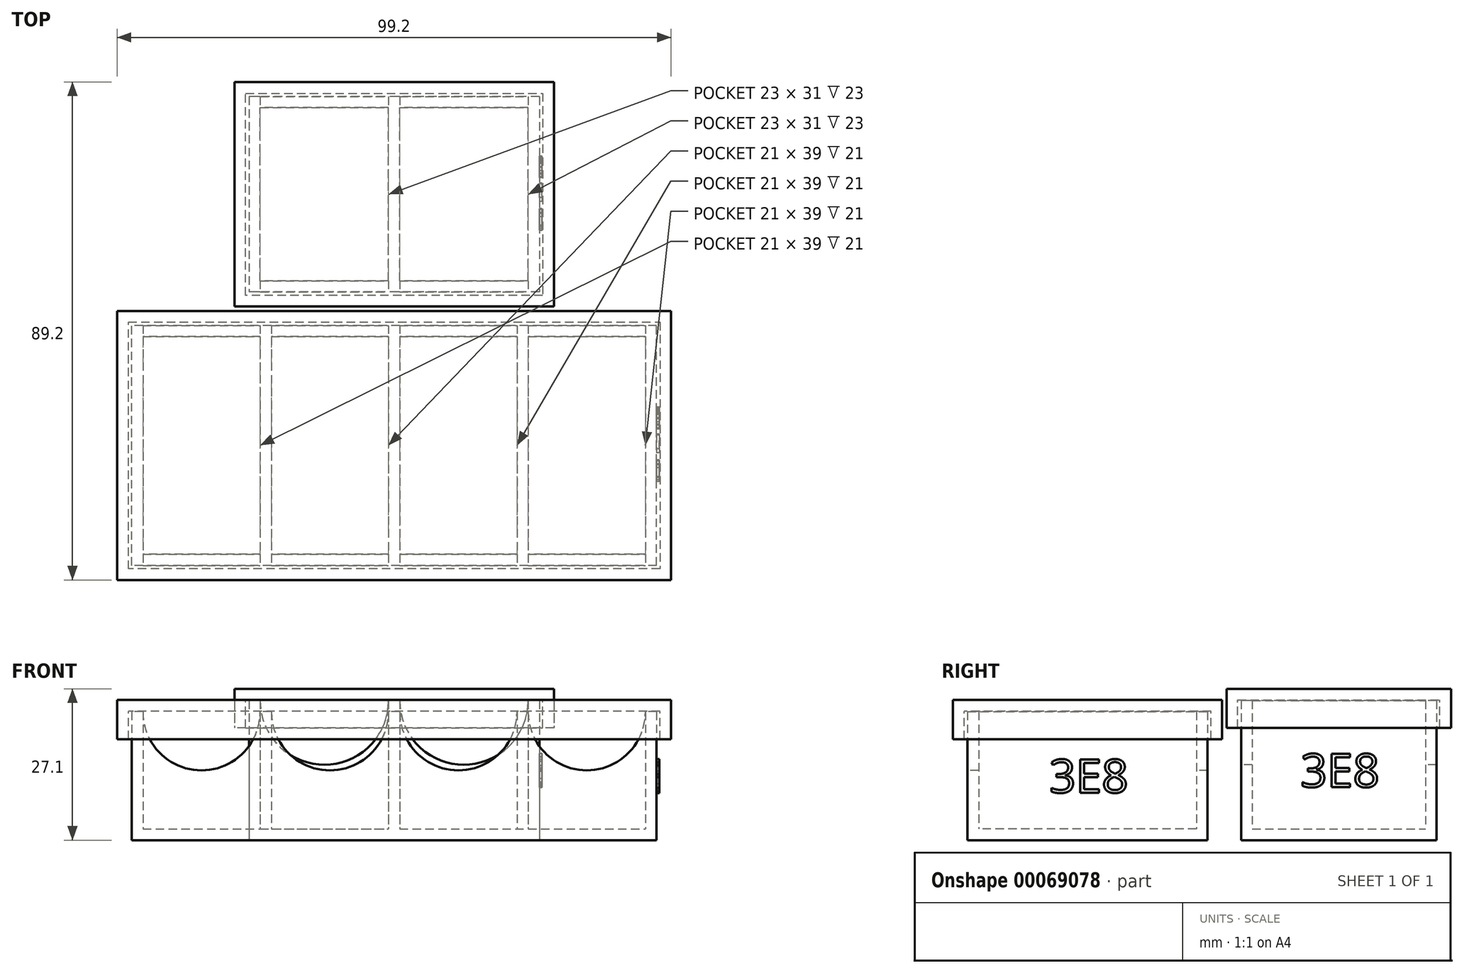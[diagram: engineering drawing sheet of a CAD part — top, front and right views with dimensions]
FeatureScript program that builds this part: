
annotation { "Feature Type Name" : "Feature", "Feature Type Description" : "" }
export const myFeature = defineFeature(function(context is Context, id is Id, definition is map)
    precondition{}
    {
        {
            var Q0;
            Q0=qCreatedBy(makeId("Top.planeOp"),FACE);
            var sketch = newSketch(context, id + "F0", { "sketchPlane" : qUnion([Q0])});
            skLineSegment(sketch, "E0.rect.bottom", {"start": v(47, -21.5) * mm, "end": v(-47, -21.5) * mm});
            skLineSegment(sketch, "E0.rect.top", {"start": v(47, 21.5) * mm, "end": v(-47, 21.5) * mm});
            skLineSegment(sketch, "E0.rect.left", {"start": v(47, -21.5) * mm, "end": v(47, 21.5) * mm});
            skLineSegment(sketch, "E0.rect.right", {"start": v(-47, -21.5) * mm, "end": v(-47, 21.5) * mm});
            skPoint(sketch, "E0.rect.middle", {"position": v(0, 0) * mm});
            skLineSegment(sketch, "E1", {"start": v(0, 0) * mm, "end": v(0, 45) * mm, "construction": true});
            skLineSegment(sketch, "E2.rect.bottom", {"start": v(26, 62.5) * mm, "end": v(-26, 62.5) * mm});
            skLineSegment(sketch, "E2.rect.top", {"start": v(26, 27.5) * mm, "end": v(-26, 27.5) * mm});
            skLineSegment(sketch, "E2.rect.left", {"start": v(26, 62.5) * mm, "end": v(26, 27.5) * mm});
            skLineSegment(sketch, "E2.rect.right", {"start": v(-26, 62.5) * mm, "end": v(-26, 27.5) * mm});
            skPoint(sketch, "E2.rect.middle", {"position": v(0, 45) * mm});
            skSolve(sketch);
        }
        {
            var Q0;
            Q0=qSketchRegion(id+"F0",true);
            extrude(context, id + "F1", {"entities" : qUnion([Q0]), "depth" : 2 * mm});
        }
        {
            var Q0;
            Q0=makeQuery(id+"F1.opExtrude","CAP_FACE",FACE,{"disambiguationData":[OSD([sQuery(id+"F0.wireOp",EDGE,"E0.rect.bottom"),sQuery(id+"F0.wireOp",EDGE,"E0.rect.top"),sQuery(id+"F0.wireOp",EDGE,"E0.rect.left"),sQuery(id+"F0.wireOp",EDGE,"E0.rect.right")])],"isStart":false});
            var sketch = newSketch(context, id + "F2", { "sketchPlane" : qUnion([Q0])});
            skLineSegment(sketch, "E3.0.0", {"start": v(-47, -21.5) * mm, "end": v(47, -21.5) * mm});
            skLineSegment(sketch, "E3.0.1", {"start": v(47, -21.5) * mm, "end": v(47, 21.5) * mm});
            skLineSegment(sketch, "E3.0.2", {"start": v(47, 21.5) * mm, "end": v(-47, 21.5) * mm});
            skLineSegment(sketch, "E3.0.3", {"start": v(-47, 21.5) * mm, "end": v(-47, -21.5) * mm});
            skLineSegment(sketch, "E4", {"start": v(-47, 0) * mm, "end": v(-45, 0) * mm, "construction": true});
            skLineSegment(sketch, "E5.bottom", {"start": v(-45, 19.5) * mm, "end": v(-24, 19.5) * mm});
            skLineSegment(sketch, "E5.top", {"start": v(-45, -19.5) * mm, "end": v(-24, -19.5) * mm});
            skLineSegment(sketch, "E5.left", {"start": v(-45, 19.5) * mm, "end": v(-45, -19.5) * mm});
            skLineSegment(sketch, "E5.right", {"start": v(-24, 19.5) * mm, "end": v(-24, -19.5) * mm});
            skLineSegment(sketch, "E6.1.0.0", {"start": v(-1, 19.5) * mm, "end": v(-1, -19.5) * mm});
            skLineSegment(sketch, "E6.1.0.1", {"start": v(-22, 19.5) * mm, "end": v(-1, 19.5) * mm});
            skLineSegment(sketch, "E6.1.0.2", {"start": v(-22, 19.5) * mm, "end": v(-22, -19.5) * mm});
            skLineSegment(sketch, "E6.1.0.3", {"start": v(-22, -19.5) * mm, "end": v(-1, -19.5) * mm});
            skLineSegment(sketch, "E6.2.0.0", {"start": v(22, 19.5) * mm, "end": v(22, -19.5) * mm});
            skLineSegment(sketch, "E6.2.0.1", {"start": v(1, 19.5) * mm, "end": v(22, 19.5) * mm});
            skLineSegment(sketch, "E6.2.0.2", {"start": v(1, 19.5) * mm, "end": v(1, -19.5) * mm});
            skLineSegment(sketch, "E6.2.0.3", {"start": v(1, -19.5) * mm, "end": v(22, -19.5) * mm});
            skLineSegment(sketch, "E6.3.0.0", {"start": v(45, 19.5) * mm, "end": v(45, -19.5) * mm});
            skLineSegment(sketch, "E6.3.0.1", {"start": v(24, 19.5) * mm, "end": v(45, 19.5) * mm});
            skLineSegment(sketch, "E6.3.0.2", {"start": v(24, 19.5) * mm, "end": v(24, -19.5) * mm});
            skLineSegment(sketch, "E6.3.0.3", {"start": v(24, -19.5) * mm, "end": v(45, -19.5) * mm});
            skLineSegment(sketch, "E6.direction1", {"start": v(-24, -19.5) * mm, "end": v(-1, -19.5) * mm, "construction": true});
            skSolve(sketch);
        }
        {
            var Q0;
            Q0=qSketchRegion(id+"F2",true);
            extrude(context, id + "F3", {"entities" : qUnion([Q0]), "operationType" : NewBodyOperationType.ADD, "depth" : 21 * mm});
        }
        {
            var Q0;
            Q0=makeQuery(id+"F3.boolean.opBoolean","MERGE",FACE,{"derivedFrom":[makeQuery(id+"F1.opExtrude","SWEPT_FACE",FACE,{"disambiguationData":[OSD([sQuery(id+"F0.wireOp",EDGE,"E0.rect.bottom")])]}),makeQuery(id+"F3.opExtrude","SWEPT_FACE",FACE,{"disambiguationData":[OSD([sQuery(id+"F2.wireOp",EDGE,"E3.0.0")])]})]});
            var sketch = newSketch(context, id + "F4", { "sketchPlane" : qUnion([Q0])});
            skPoint(sketch, "E7.0", {"position": v(-45, 23) * mm});
            skPoint(sketch, "E8.0", {"position": v(-24, 23) * mm});
            skLineSegment(sketch, "E9", {"start": v(-45, 23) * mm, "end": v(-24, 23) * mm});
            skArc(sketch, "E10", {"start": v(-45, 23) * mm, "mid": v(-34.5, 12.5) * mm, "end": v(-24, 23) * mm});
            skLineSegment(sketch, "E11.1.0.0", {"start": v(-22, 23) * mm, "end": v(-1, 23) * mm});
            skArc(sketch, "E11.1.0.1", {"start": v(-22, 23) * mm, "mid": v(-11.5, 12.5) * mm, "end": v(-1, 23) * mm});
            skLineSegment(sketch, "E11.2.0.0", {"start": v(1, 23) * mm, "end": v(22, 23) * mm});
            skArc(sketch, "E11.2.0.1", {"start": v(1, 23) * mm, "mid": v(11.5, 12.5) * mm, "end": v(22, 23) * mm});
            skLineSegment(sketch, "E11.3.0.0", {"start": v(24, 23) * mm, "end": v(45, 23) * mm});
            skArc(sketch, "E11.3.0.1", {"start": v(24, 23) * mm, "mid": v(34.5, 12.5) * mm, "end": v(45, 23) * mm});
            skLineSegment(sketch, "E11.direction1", {"start": v(-45, 23) * mm, "end": v(-22, 23) * mm, "construction": true});
            skSolve(sketch);
        }
        {
            var Q0;
            Q0=qSketchRegion(id+"F4",true);
            extrude(context, id + "F5", {"entities" : qUnion([Q0]), "operationType" : NewBodyOperationType.REMOVE, "endBound" : BoundingType.THROUGH_ALL, "oppositeDirection" : true, "depth" : 25 * mm});
        }
        {
            var Q0;
            {var subQ0=sQuery(id+"F2.wireOp",EDGE,"E3.0.0");var subQ1=sQuery(id+"F2.wireOp",EDGE,"E5.bottom");var subQ2=sQuery(id+"F2.wireOp",EDGE,"E3.0.2");var subQ3=sQuery(id+"F2.wireOp",EDGE,"E3.0.3");var subQ4=sQuery(id+"F2.wireOp",EDGE,"E5.top");var subQ5=sQuery(id+"F2.wireOp",EDGE,"E5.left");Q0=makeQuery(id+"F5.boolean.opBoolean","SPLIT",FACE,{"disambiguationData":[TD([makeQuery(id+"F1.opExtrude","SWEPT_FACE",FACE,{"disambiguationData":[OSD([sQuery(id+"F0.wireOp",EDGE,"E0.rect.right")])]})])],"derivedFrom":makeQuery(id+"F3.opExtrude","CAP_FACE",FACE,{"disambiguationData":[OSD([subQ0,sQuery(id+"F2.wireOp",EDGE,"E3.0.1"),subQ2,subQ3,subQ1,subQ4,subQ5,sQuery(id+"F2.wireOp",EDGE,"E5.right"),sQuery(id+"F2.wireOp",EDGE,"E6.1.0.0"),sQuery(id+"F2.wireOp",EDGE,"E6.1.0.1"),sQuery(id+"F2.wireOp",EDGE,"E6.1.0.2"),sQuery(id+"F2.wireOp",EDGE,"E6.1.0.3"),sQuery(id+"F2.wireOp",EDGE,"E6.2.0.0"),sQuery(id+"F2.wireOp",EDGE,"E6.2.0.1"),sQuery(id+"F2.wireOp",EDGE,"E6.2.0.2"),sQuery(id+"F2.wireOp",EDGE,"E6.2.0.3"),sQuery(id+"F2.wireOp",EDGE,"E6.3.0.0"),sQuery(id+"F2.wireOp",EDGE,"E6.3.0.1"),sQuery(id+"F2.wireOp",EDGE,"E6.3.0.2"),sQuery(id+"F2.wireOp",EDGE,"E6.3.0.3"),sQuery(id+"F2.wireOp",EDGE,"E6.4.0.0"),sQuery(id+"F2.wireOp",EDGE,"E6.4.0.1"),sQuery(id+"F2.wireOp",EDGE,"E6.4.0.2"),sQuery(id+"F2.wireOp",EDGE,"E6.4.0.3"),sQuery(id+"F2.wireOp",EDGE,"E6.5.0.0"),sQuery(id+"F2.wireOp",EDGE,"E6.5.0.1"),sQuery(id+"F2.wireOp",EDGE,"E6.5.0.2"),sQuery(id+"F2.wireOp",EDGE,"E6.5.0.3")])],"isStart":false})});}
            cPlane(context, id + "F6", {"entities" : qUnion([Q0]), "cplaneType" : CPlaneType.OFFSET, "offset" : .1 * mm, "width" : 150 * mm, "height" : 150 * mm});
        }
        {
            var Q0;
            Q0=qCreatedBy(id+"F6.planeOp",FACE);
            var sketch = newSketch(context, id + "F7", { "sketchPlane" : qUnion([Q0])});
            skLineSegment(sketch, "E12.0.0", {"start": v(47, -21.5) * mm, "end": v(-47, -21.5) * mm, "construction": true});
            skLineSegment(sketch, "E12.0.1", {"start": v(-47, -21.5) * mm, "end": v(-47, 21.5) * mm, "construction": true});
            skLineSegment(sketch, "E12.0.2", {"start": v(-47, 21.5) * mm, "end": v(47, 21.5) * mm});
            skLineSegment(sketch, "E12.0.3", {"start": v(47, 21.5) * mm, "end": v(47, -21.5) * mm, "construction": true});
            skLineSegment(sketch, "E13.0", {"start": v(-49.6, 24.1) * mm, "end": v(49.6, 24.1) * mm});
            skLineSegment(sketch, "E13.1", {"start": v(-49.6, -24.1) * mm, "end": v(-49.6, 24.1) * mm});
            skLineSegment(sketch, "E13.2", {"start": v(49.6, -24.1) * mm, "end": v(-49.6, -24.1) * mm});
            skLineSegment(sketch, "E13.3", {"start": v(49.6, 24.1) * mm, "end": v(49.6, -24.1) * mm});
            skSolve(sketch);
        }
        {
            var Q0;
            Q0=qSketchRegion(id+"F7",true);
            extrude(context, id + "F8", {"entities" : qUnion([Q0]), "depth" : 2 * mm});
        }
        {
            var Q0;
            Q0=makeQuery(id+"F8.opExtrude","CAP_FACE",FACE,{"disambiguationData":[OSD([sQuery(id+"F7.wireOp",EDGE,"E13.0"),sQuery(id+"F7.wireOp",EDGE,"E13.1"),sQuery(id+"F7.wireOp",EDGE,"E13.2"),sQuery(id+"F7.wireOp",EDGE,"E13.3")])],"isStart":true});
            var sketch = newSketch(context, id + "F9", { "sketchPlane" : qUnion([Q0])});
            skLineSegment(sketch, "E14.0.0", {"start": v(-49.6, -24.1) * mm, "end": v(49.6, -24.1) * mm});
            skLineSegment(sketch, "E14.0.1", {"start": v(49.6, -24.1) * mm, "end": v(49.6, 24.1) * mm});
            skLineSegment(sketch, "E14.0.2", {"start": v(49.6, 24.1) * mm, "end": v(-49.6, 24.1) * mm});
            skLineSegment(sketch, "E14.0.3", {"start": v(-49.6, 24.1) * mm, "end": v(-49.6, -24.1) * mm});
            skLineSegment(sketch, "E15.0", {"start": v(47.6, 22.1) * mm, "end": v(-47.6, 22.1) * mm});
            skLineSegment(sketch, "E15.1", {"start": v(47.6, -22.1) * mm, "end": v(47.6, 22.1) * mm});
            skLineSegment(sketch, "E15.2", {"start": v(-47.6, -22.1) * mm, "end": v(47.6, -22.1) * mm});
            skLineSegment(sketch, "E15.3", {"start": v(-47.6, 22.1) * mm, "end": v(-47.6, -22.1) * mm});
            skSolve(sketch);
        }
        {
            var Q0;
            Q0=qSketchRegion(id+"F9",true);
            extrude(context, id + "F10", {"entities" : qUnion([Q0]), "operationType" : NewBodyOperationType.ADD, "depth" : 5 * mm});
        }
        {
            var Q0;
            Q0=makeQuery(id+"F1.opExtrude","CAP_FACE",FACE,{"disambiguationData":[OSD([sQuery(id+"F0.wireOp",EDGE,"E2.rect.bottom"),sQuery(id+"F0.wireOp",EDGE,"E2.rect.top"),sQuery(id+"F0.wireOp",EDGE,"E2.rect.left"),sQuery(id+"F0.wireOp",EDGE,"E2.rect.right")])],"isStart":false});
            var sketch = newSketch(context, id + "F11", { "sketchPlane" : qUnion([Q0])});
            skLineSegment(sketch, "E16.0.0", {"start": v(26, 27.5) * mm, "end": v(26, 62.5) * mm});
            skLineSegment(sketch, "E16.0.1", {"start": v(26, 62.5) * mm, "end": v(-26, 62.5) * mm});
            skLineSegment(sketch, "E16.0.2", {"start": v(-26, 62.5) * mm, "end": v(-26, 27.5) * mm});
            skLineSegment(sketch, "E16.0.3", {"start": v(-26, 27.5) * mm, "end": v(26, 27.5) * mm});
            skLineSegment(sketch, "E17", {"start": v(-26, 45) * mm, "end": v(-24, 45) * mm, "construction": true});
            skLineSegment(sketch, "E18.bottom", {"start": v(-24, 29.5) * mm, "end": v(-1, 29.5) * mm});
            skLineSegment(sketch, "E18.top", {"start": v(-24, 60.5) * mm, "end": v(-1, 60.5) * mm});
            skLineSegment(sketch, "E18.left", {"start": v(-24, 29.5) * mm, "end": v(-24, 60.5) * mm});
            skLineSegment(sketch, "E18.right", {"start": v(-1, 29.5) * mm, "end": v(-1, 60.5) * mm});
            skLineSegment(sketch, "E19.1.0.0", {"start": v(1, 29.5) * mm, "end": v(24, 29.5) * mm});
            skLineSegment(sketch, "E19.1.0.1", {"start": v(1, 29.5) * mm, "end": v(1, 60.5) * mm});
            skLineSegment(sketch, "E19.1.0.2", {"start": v(1, 60.5) * mm, "end": v(24, 60.5) * mm});
            skLineSegment(sketch, "E19.1.0.3", {"start": v(24, 29.5) * mm, "end": v(24, 60.5) * mm});
            skLineSegment(sketch, "E19.direction1", {"start": v(-24, 29.5) * mm, "end": v(1, 29.5) * mm, "construction": true});
            skSolve(sketch);
        }
        {
            var Q0;
            Q0=qSketchRegion(id+"F11",true);
            extrude(context, id + "F12", {"entities" : qUnion([Q0]), "operationType" : NewBodyOperationType.ADD, "depth" : 23 * mm});
        }
        {
            var Q0;
            Q0=makeQuery(id+"F12.boolean.opBoolean","MERGE",FACE,{"derivedFrom":[makeQuery(id+"F1.opExtrude","SWEPT_FACE",FACE,{"disambiguationData":[OSD([sQuery(id+"F0.wireOp",EDGE,"E2.rect.top")])]}),makeQuery(id+"F12.opExtrude","SWEPT_FACE",FACE,{"disambiguationData":[OSD([sQuery(id+"F11.wireOp",EDGE,"E16.0.3")])]})]});
            var sketch = newSketch(context, id + "F13", { "sketchPlane" : qUnion([Q0])});
            skPoint(sketch, "E20.0", {"position": v(-24, 25) * mm});
            skPoint(sketch, "E21.0", {"position": v(-1, 25) * mm});
            skLineSegment(sketch, "E22", {"start": v(-24, 25) * mm, "end": v(-1, 25) * mm});
            skArc(sketch, "E23", {"start": v(-24, 25) * mm, "mid": v(-12.5, 13.5) * mm, "end": v(-1, 25) * mm});
            skArc(sketch, "E24.1.0.0", {"start": v(1, 25) * mm, "mid": v(12.5, 13.5) * mm, "end": v(24, 25) * mm});
            skLineSegment(sketch, "E24.1.0.1", {"start": v(1, 25) * mm, "end": v(24, 25) * mm});
            skLineSegment(sketch, "E24.direction1", {"start": v(-24, 25) * mm, "end": v(1, 25) * mm, "construction": true});
            skSolve(sketch);
        }
        {
            var Q0;
            Q0=qSketchRegion(id+"F13",true);
            extrude(context, id + "F14", {"entities" : qUnion([Q0]), "operationType" : NewBodyOperationType.REMOVE, "endBound" : BoundingType.THROUGH_ALL, "oppositeDirection" : true, "depth" : 25 * mm});
        }
        {
            var Q0;
            {var subQ0=sQuery(id+"F11.wireOp",EDGE,"E16.0.1");var subQ1=sQuery(id+"F11.wireOp",EDGE,"E18.bottom");var subQ2=sQuery(id+"F11.wireOp",EDGE,"E18.top");var subQ3=sQuery(id+"F11.wireOp",EDGE,"E18.left");var subQ4=sQuery(id+"F11.wireOp",EDGE,"E16.0.2");var subQ5=sQuery(id+"F11.wireOp",EDGE,"E16.0.3");Q0=makeQuery(id+"F14.boolean.opBoolean","SPLIT",FACE,{"disambiguationData":[TD([makeQuery(id+"F1.opExtrude","SWEPT_FACE",FACE,{"disambiguationData":[OSD([sQuery(id+"F0.wireOp",EDGE,"E2.rect.right")])]})])],"derivedFrom":makeQuery(id+"F12.opExtrude","CAP_FACE",FACE,{"disambiguationData":[OSD([sQuery(id+"F11.wireOp",EDGE,"E16.0.0"),subQ0,subQ4,subQ5,subQ1,subQ2,subQ3,sQuery(id+"F11.wireOp",EDGE,"E18.right"),sQuery(id+"F11.wireOp",EDGE,"E19.1.0.0"),sQuery(id+"F11.wireOp",EDGE,"E19.1.0.1"),sQuery(id+"F11.wireOp",EDGE,"E19.1.0.2"),sQuery(id+"F11.wireOp",EDGE,"E19.1.0.3"),sQuery(id+"F11.wireOp",EDGE,"E19.2.0.0"),sQuery(id+"F11.wireOp",EDGE,"E19.2.0.1"),sQuery(id+"F11.wireOp",EDGE,"E19.2.0.2"),sQuery(id+"F11.wireOp",EDGE,"E19.2.0.3"),sQuery(id+"F11.wireOp",EDGE,"E19.3.0.0"),sQuery(id+"F11.wireOp",EDGE,"E19.3.0.1"),sQuery(id+"F11.wireOp",EDGE,"E19.3.0.2"),sQuery(id+"F11.wireOp",EDGE,"E19.3.0.3")])],"isStart":false})});}
            cPlane(context, id + "F15", {"entities" : qUnion([Q0]), "cplaneType" : CPlaneType.OFFSET, "offset" : .1 * mm, "width" : 150 * mm, "height" : 150 * mm});
        }
        {
            var Q0;
            Q0=qCreatedBy(id+"F15.planeOp",FACE);
            var sketch = newSketch(context, id + "F16", { "sketchPlane" : qUnion([Q0])});
            skLineSegment(sketch, "E25.0.0", {"start": v(26, 62.5) * mm, "end": v(26, 27.5) * mm, "construction": true});
            skLineSegment(sketch, "E25.0.1", {"start": v(26, 27.5) * mm, "end": v(-26, 27.5) * mm, "construction": true});
            skLineSegment(sketch, "E25.0.2", {"start": v(-26, 27.5) * mm, "end": v(-26, 62.5) * mm, "construction": true});
            skLineSegment(sketch, "E25.0.3", {"start": v(-26, 62.5) * mm, "end": v(26, 62.5) * mm, "construction": true});
            skLineSegment(sketch, "E26.0", {"start": v(-28.6, 24.9) * mm, "end": v(-28.6, 65.1) * mm});
            skLineSegment(sketch, "E26.1", {"start": v(28.6, 24.9) * mm, "end": v(-28.6, 24.9) * mm});
            skLineSegment(sketch, "E26.2", {"start": v(28.6, 65.1) * mm, "end": v(28.6, 24.9) * mm});
            skLineSegment(sketch, "E26.3", {"start": v(-28.6, 65.1) * mm, "end": v(28.6, 65.1) * mm});
            skSolve(sketch);
        }
        {
            var Q0;
            Q0=qSketchRegion(id+"F16",true);
            extrude(context, id + "F17", {"entities" : qUnion([Q0]), "depth" : 2 * mm});
        }
        {
            var Q0;
            Q0=makeQuery(id+"F17.opExtrude","CAP_FACE",FACE,{"disambiguationData":[OSD([sQuery(id+"F16.wireOp",EDGE,"E26.0"),sQuery(id+"F16.wireOp",EDGE,"E26.1"),sQuery(id+"F16.wireOp",EDGE,"E26.2"),sQuery(id+"F16.wireOp",EDGE,"E26.3")])],"isStart":true});
            var sketch = newSketch(context, id + "F18", { "sketchPlane" : qUnion([Q0])});
            skLineSegment(sketch, "E27.0.0", {"start": v(-28.6, -24.9) * mm, "end": v(-28.6, -65.1) * mm});
            skLineSegment(sketch, "E27.0.1", {"start": v(-28.6, -65.1) * mm, "end": v(28.6, -65.1) * mm});
            skLineSegment(sketch, "E27.0.2", {"start": v(28.6, -65.1) * mm, "end": v(28.6, -24.9) * mm});
            skLineSegment(sketch, "E27.0.3", {"start": v(28.6, -24.9) * mm, "end": v(-28.6, -24.9) * mm});
            skLineSegment(sketch, "E28.0", {"start": v(-26.6, -63.1) * mm, "end": v(26.6, -63.1) * mm});
            skLineSegment(sketch, "E28.1", {"start": v(-26.6, -26.9) * mm, "end": v(-26.6, -63.1) * mm});
            skLineSegment(sketch, "E28.2", {"start": v(26.6, -26.9) * mm, "end": v(-26.6, -26.9) * mm});
            skLineSegment(sketch, "E28.3", {"start": v(26.6, -63.1) * mm, "end": v(26.6, -26.9) * mm});
            skSolve(sketch);
        }
        {
            var Q0;
            Q0=qSketchRegion(id+"F18",true);
            extrude(context, id + "F19", {"entities" : qUnion([Q0]), "operationType" : NewBodyOperationType.ADD, "depth" : 5 * mm});
        }
        {
            var Q0;
            Q0=makeQuery(id+"F3.boolean.opBoolean","MERGE",FACE,{"derivedFrom":[makeQuery(id+"F1.opExtrude","SWEPT_FACE",FACE,{"disambiguationData":[OSD([sQuery(id+"F0.wireOp",EDGE,"E0.rect.left")])]}),makeQuery(id+"F3.opExtrude","SWEPT_FACE",FACE,{"disambiguationData":[OSD([sQuery(id+"F2.wireOp",EDGE,"E3.0.1")])]})]});
            var sketch = newSketch(context, id + "F20", { "sketchPlane" : qUnion([Q0])});
            skText(sketch, "E29", { "text": "3E8", "fontName": "OpenSans-Regular.ttf"});
            skLineSegment(sketch, "E30", {"start": v(-21.5, 23) * mm, "end": v(21.5, 0) * mm, "construction": true});
            skPoint(sketch, "E31", {"position": v(0, 11.5) * mm});
            const initialGuessF20  = {"E29": [-0.00687, 0.0085, 1, 0, 0.006]};
            skSetInitialGuess(sketch, initialGuessF20);
            skSolve(sketch);
        }
        {
            var Q0;
            Q0=qSketchRegion(id+"F20",true);
            extrude(context, id + "F21", {"entities" : qUnion([Q0]), "operationType" : NewBodyOperationType.ADD, "depth" : .5 * mm});
        }
        {
            var Q0;
            Q0=makeQuery(id+"F12.boolean.opBoolean","MERGE",FACE,{"derivedFrom":[makeQuery(id+"F1.opExtrude","SWEPT_FACE",FACE,{"disambiguationData":[OSD([sQuery(id+"F0.wireOp",EDGE,"E2.rect.left")])]}),makeQuery(id+"F12.opExtrude","SWEPT_FACE",FACE,{"disambiguationData":[OSD([sQuery(id+"F11.wireOp",EDGE,"E16.0.0")])]})]});
            var sketch = newSketch(context, id + "F22", { "sketchPlane" : qUnion([Q0])});
            skText(sketch, "E32", { "text": "3E8", "fontName": "OpenSans-Regular.ttf"});
            skPoint(sketch, "E33", {"position": v(45, 12.5) * mm});
            skLineSegment(sketch, "E34", {"start": v(27.5, 25) * mm, "end": v(62.5, 0) * mm, "construction": true});
            const initialGuessF22  = {"E32": [0.03813, 0.0095, 1, 0, 0.006]};
            skSetInitialGuess(sketch, initialGuessF22);
            skSolve(sketch);
        }
        {
            var Q0;
            Q0=qSketchRegion(id+"F22",true);
            extrude(context, id + "F23", {"entities" : qUnion([Q0]), "operationType" : NewBodyOperationType.ADD, "depth" : .5 * mm});
        }
    });
